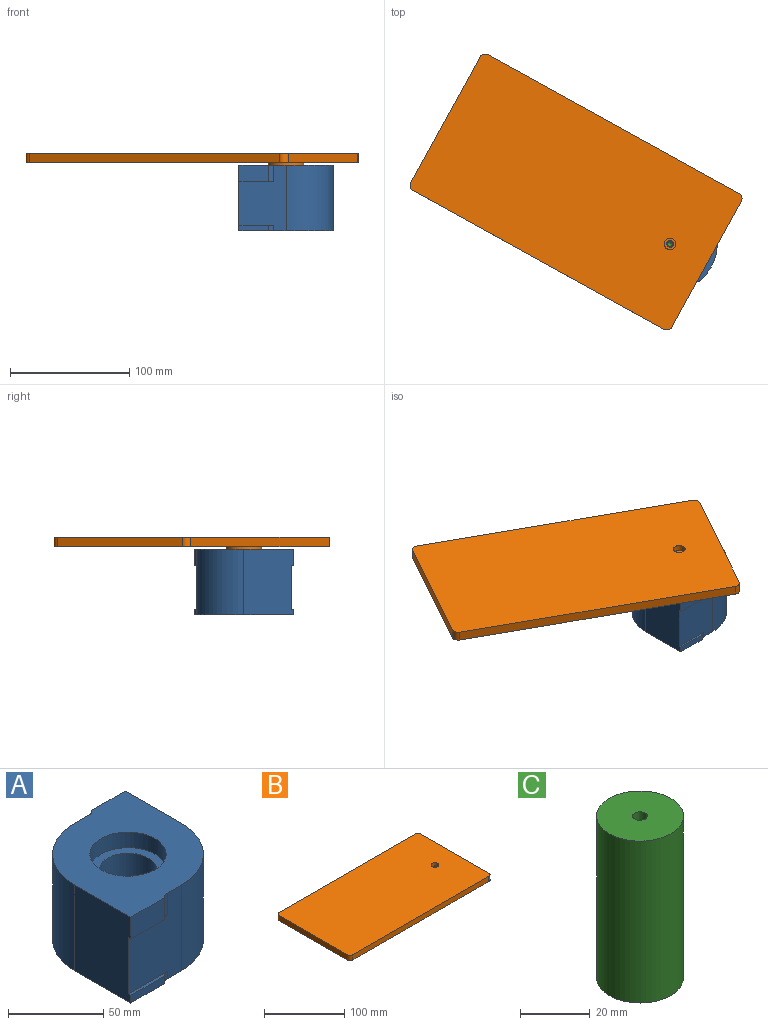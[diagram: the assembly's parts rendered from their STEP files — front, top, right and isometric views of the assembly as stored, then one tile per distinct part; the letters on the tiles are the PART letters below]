
ASSEMBLY  parts=3 mates=4
PART A: 25 faces, bbox 79x83x55 mm
  f0: cylinder r=15mm len=35mm, axis (0,0,1), area 3298.7mm2, adj f21,f23
  f1: plane 55x39.5mm, normal (0,1,0), area 1627.3mm2, adj f3,f5,f6,f8,f13,f15,f17,f18
  f2: plane 55x39.5mm, normal (0,-1,0), area 1627.3mm2, adj f4,f5,f6,f7,f9,f11,f19,f20
  f3: plane 55x41.5mm, normal (1,0,0), area 2210.1mm2, adj f1,f5,f6,f7,f13,f14,f15,f16
  f4: plane 55x41.5mm, normal (-1,0,0), area 2210.1mm2, adj f2,f5,f6,f8,f9,f10,f11,f12
  f5: plane 83x79mm, normal (0,0,1), area 4419.5mm2, adj f1,f2,f3,f4,f7,f8,f10,f14
  f6: plane 83x79mm, normal (0,0,-1), area 4419.5mm2, adj f1,f2,f3,f4,f7,f8,f12,f16
  f7: cylinder r=39.5mm len=55mm, axis (0,0,1), area 3412.6mm2, adj f2,f3,f5,f6
  f8: cylinder r=39.5mm len=55mm, axis (0,0,1), area 3412.6mm2, adj f1,f4,f5,f6
  f9: plane 29x2mm, normal (0,0,-1), area 52.4mm2, adj f2,f4,f10,f20
  f10: plane 25x14mm, normal (0,-1,0), area 350mm2, adj f4,f5,f9,f20
  f11: plane 29x2mm, normal (0,0,1), area 52.4mm2, adj f2,f4,f12,f19
  f12: plane 25x4.8mm, normal (0,-1,0), area 120mm2, adj f4,f6,f11,f19
  f13: plane 29x2mm, normal (0,0,-1), area 52.4mm2, adj f1,f3,f14,f18
  f14: plane 25x14mm, normal (0,1,0), area 350mm2, adj f3,f5,f13,f18
  f15: plane 29x2mm, normal (0,0,1), area 52.4mm2, adj f1,f3,f16,f17
  f16: plane 25x4.8mm, normal (0,1,0), area 120mm2, adj f3,f6,f15,f17
  f17: cylinder r=5mm len=4.8mm, axis (0,0,1), area 22.3mm2, adj f1,f6,f15,f16
  f18: cylinder r=5mm len=14mm, axis (0,0,-1), area 64.9mm2, adj f1,f5,f13,f14
  f19: cylinder r=5mm len=4.8mm, axis (0,0,1), area 22.3mm2, adj f2,f6,f11,f12
  f20: cylinder r=5mm len=14mm, axis (0,0,-1), area 64.9mm2, adj f2,f5,f9,f10
  f21: plane 40x40mm, normal (0,0,1), area 549.8mm2, adj f0,f22
  f22: cylinder r=20mm len=40mm, axis (0,0,1), area 1256.6mm2, adj f5,f21
  f23: plane 40x40mm, normal (0,0,-1), area 549.8mm2, adj f0,f24
  f24: cylinder r=20mm len=40mm, axis (0,0,-1), area 1256.6mm2, adj f6,f23
PART B: 17 faces, bbox 250x130x10 mm
  f0: plane 240x8mm, normal (0,-1,0), area 1920mm2, adj f4,f5,f6,f9
  f1: plane 120x8mm, normal (1,0,0), area 960mm2, adj f4,f5,f6,f7
  f2: plane 240x8mm, normal (0,1,0), area 1920mm2, adj f4,f5,f7,f8
  f3: plane 120x8mm, normal (-1,0,0), area 960mm2, adj f4,f5,f8,f9
  f4: plane 250x130mm, normal (0,0,1), area 32403.9mm2, adj f0,f1,f2,f3,f6,f7,f8,f9
  f5: plane 250x130mm, normal (0,0,-1), area 31771.7mm2, adj f0,f1,f2,f3,f6,f7,f8,f9
  f6: cylinder r=5mm len=8mm, axis (0,0,1), area 62.8mm2, adj f0,f1,f4,f5
  f7: cylinder r=5mm len=8mm, axis (0,0,-1), area 62.8mm2, adj f1,f2,f4,f5
  f8: cylinder r=5mm len=8mm, axis (0,0,1), area 62.8mm2, adj f2,f3,f4,f5
  f9: cylinder r=5mm len=8mm, axis (0,0,-1), area 62.8mm2, adj f0,f3,f4,f5
  f10: cylinder r=15mm len=30mm, axis (0,0,1), area 188.5mm2, adj f5,f11
  f11: plane 30x30mm, normal (0,0,-1), area 216mm2, adj f10,f12
  f12: cylinder r=12.5mm len=25mm, axis (0,0,-1), area 157.1mm2, adj f11,f13
  f13: plane 25x25mm, normal (0,0,-1), area 467.1mm2, adj f12,f14
  f14: cylinder r=2.75mm len=5.5mm, axis (0,0,1), area 51.8mm2, adj f13,f15
  f15: plane 9.75x9.75mm, normal (0,0,1), area 50.9mm2, adj f14,f16
  f16: cylinder r=4.88mm len=9.75mm, axis (0,0,1), area 153.2mm2, adj f4,f15
PART C: 5 faces, bbox 25x25x57 mm
  f0: cylinder r=12.5mm len=57mm, axis (0,0,-1), area 4476.8mm2, adj f1,f2
  f1: plane 25x25mm, normal (0,0,1), area 477mm2, adj f0,f4
  f2: plane 25x25mm, normal (0,0,-1), area 490.9mm2, adj f0
  f3: cone r=0mm half-angle=59deg, axis (0,0,1), area 16.2mm2, adj f4
  f4: cylinder r=2.1mm len=14.4mm, axis (0,0,1), area 190mm2, adj f1,f3
PLACE A at identity fixed
PLACE B rot(axis=(0,0,-1),28.9deg) t=(-78.79,43.5,29.5)mm
PLACE C rot(axis=(0,0,1),8.7deg) t=(0,0,1)mm
MATE cylindrical B.f12 <-> C.f0  axis (0,0,-1) through (0,0,27.5)mm
MATE planar B.f10 <-> A.f24  axis (0,0,-1) through (0,0,27.5)mm
MATE cylindrical A.f22 <-> C.f0  axis (0,0,1) through (0,0,22.5)mm
MATE planar C.f0 <-> B.f12  axis (0,0,1) through (0,0,29.5)mm
